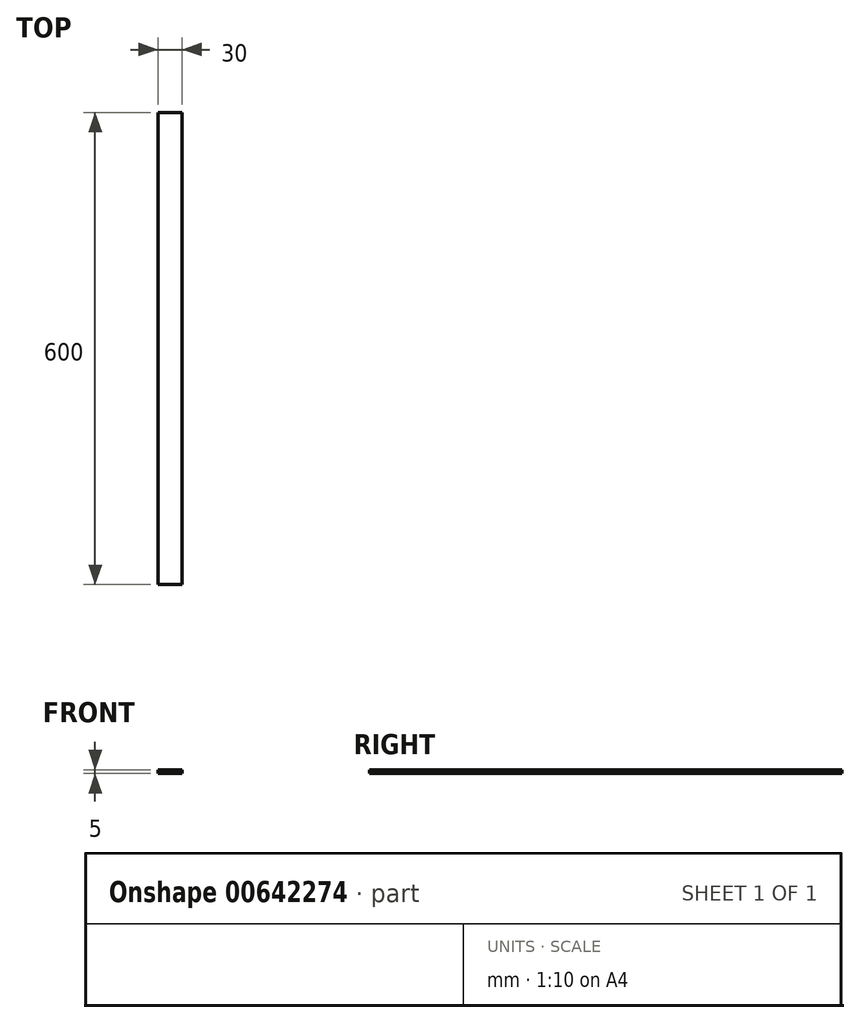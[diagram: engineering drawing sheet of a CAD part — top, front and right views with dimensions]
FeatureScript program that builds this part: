
annotation { "Feature Type Name" : "Feature", "Feature Type Description" : "" }
export const myFeature = defineFeature(function(context is Context, id is Id, definition is map)
    precondition{}
    {
        {
            var Q0;
            Q0=qCreatedBy(makeId("Front.planeOp"),FACE);
            var sketch = newSketch(context, id + "F0", { "sketchPlane" : qUnion([Q0])});
            skLineSegment(sketch, "E0.bottom", {"start": v(16.2, -2.5) * mm, "end": v(-13.8, -2.5) * mm});
            skLineSegment(sketch, "E0.top", {"start": v(16.2, 2.5) * mm, "end": v(-13.8, 2.5) * mm});
            skLineSegment(sketch, "E0.left", {"start": v(16.2, -2.5) * mm, "end": v(16.2, 2.5) * mm});
            skLineSegment(sketch, "E0.right", {"start": v(-13.8, -2.5) * mm, "end": v(-13.8, 2.5) * mm});
            skPoint(sketch, "E0.middle", {"position": v(1.2, 0) * mm});
            skSolve(sketch);
        }
        {
            var Q0;
            Q0=makeQuery(id+"F0.imprint","IMPRINT",FACE,{"disambiguationData":[TD([[makeQuery(id+"F0.imprint","IMPRINT",EDGE,{"derivedFrom":sQuery(id+"F0.wireOp",EDGE,"E0.bottom")}),-1.0]])]});
            extrude(context, id + "F1", {"entities" : qUnion([Q0]), "depth" : 600 * mm, "offsetDistance" : 25 * mm});
        }
    });
